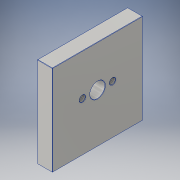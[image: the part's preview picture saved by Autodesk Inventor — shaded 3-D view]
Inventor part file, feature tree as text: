
AUTODESK INVENTOR PART (.ipt)
format: ipt  version: 2016 (Build 200138000, 138)  size: 144,384 bytes
history: native  units: in
note: dims shown in document units (in); Inventor stores cm internally (conversion verified against a paired STEP export)
features: extrude x3, sketch x3, thread x2, chamfer x1
ambient origin geometry x8: Origin, YZ Plane, XZ Plane, XY Plane, X Axis, Y Axis, Z Axis, Center Point
bodies: Solid1 (feature_tree)
feature tree (9):
  extrude  "Extrusion1"  Depth=3.0in
  extrude  "Extrusion2"  Depth=0.1in
  extrude  "Extrusion3"  Depth=0.25in
  thread  "Thread1"  [1 undecoded]
  thread  "Thread2"  [1 undecoded]
  chamfer  "Chamfer1"  Distance=0.25in
  sketch  "Sketch1"  dims[d0=0.5in d1=3.0in]
  sketch  "Sketch2"  dims[d2=3.0in d3=0.0in d4=0.1in]
  sketch  "Sketch3"  dims[d5=0.1in d6=1.0in d8=1.0in d9=0.25in d10=0.25in d11=0.0in d12=0.5in d13=0.2in d15=1.5in d16=1.0in d17=0.7874in d19=360.0deg d21=1.625in d22=0.25in d23=0.0in d24=1.0in d25=0.0in d26=1.0in d27=0.0in d28=0.01in d29=0.125in d30=45.0deg]
note: 2 required parameter values undecoded (feature->parameter linkage not recoverable at this tier; creation-order binding heuristic only, values carry confidence <= 0.55)
